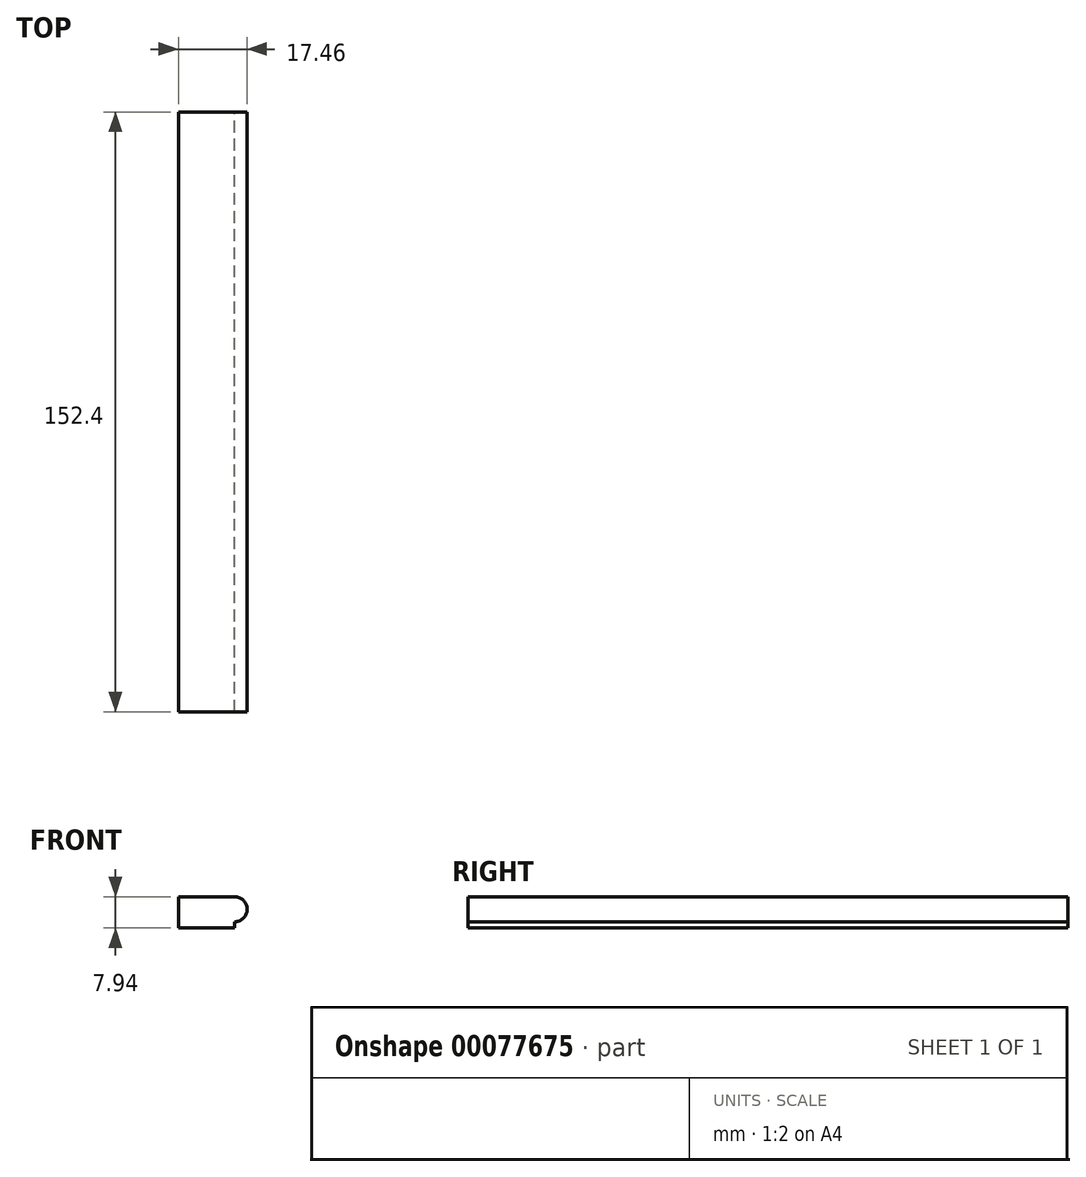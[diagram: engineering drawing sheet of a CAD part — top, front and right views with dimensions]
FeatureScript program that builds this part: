
annotation { "Feature Type Name" : "Feature", "Feature Type Description" : "" }
export const myFeature = defineFeature(function(context is Context, id is Id, definition is map)
    precondition{}
    {
        {
            var Q0;
            Q0=qCreatedBy(makeId("Front.planeOp"),FACE);
            var sketch = newSketch(context, id + "F0", { "sketchPlane" : qUnion([Q0])});
            skLineSegment(sketch, "E0", {"start": v(-8.73, -3.97) * mm, "end": v(-8.73, 3.97) * mm});
            skLineSegment(sketch, "E1", {"start": v(-8.73, 3.97) * mm, "end": v(5.56, 3.97) * mm});
            skLineSegment(sketch, "E2", {"start": v(5.56, -2.38) * mm, "end": v(5.56, -3.97) * mm});
            skLineSegment(sketch, "E3", {"start": v(5.56, -3.97) * mm, "end": v(-8.73, -3.97) * mm});
            skArc(sketch, "E4", {"start": v(5.56, -2.38) * mm, "mid": v(7.8, -1.45) * mm, "end": v(8.73, 0.8) * mm});
            skArc(sketch, "E5", {"start": v(8.73, 0.8) * mm, "mid": v(7.8, 3.04) * mm, "end": v(5.56, 3.97) * mm});
            skSolve(sketch);
        }
        {
            var Q0;
            Q0=makeQuery(id+"F0.imprint","IMPRINT",FACE,{"disambiguationData":[TD([[makeQuery(id+"F0.imprint","IMPRINT",EDGE,{"derivedFrom":sQuery(id+"F0.wireOp",EDGE,"E0")}),-1.0]])]});
            extrude(context, id + "F1", {"entities" : qUnion([Q0]), "depth" : 152.4 * mm});
        }
    });
